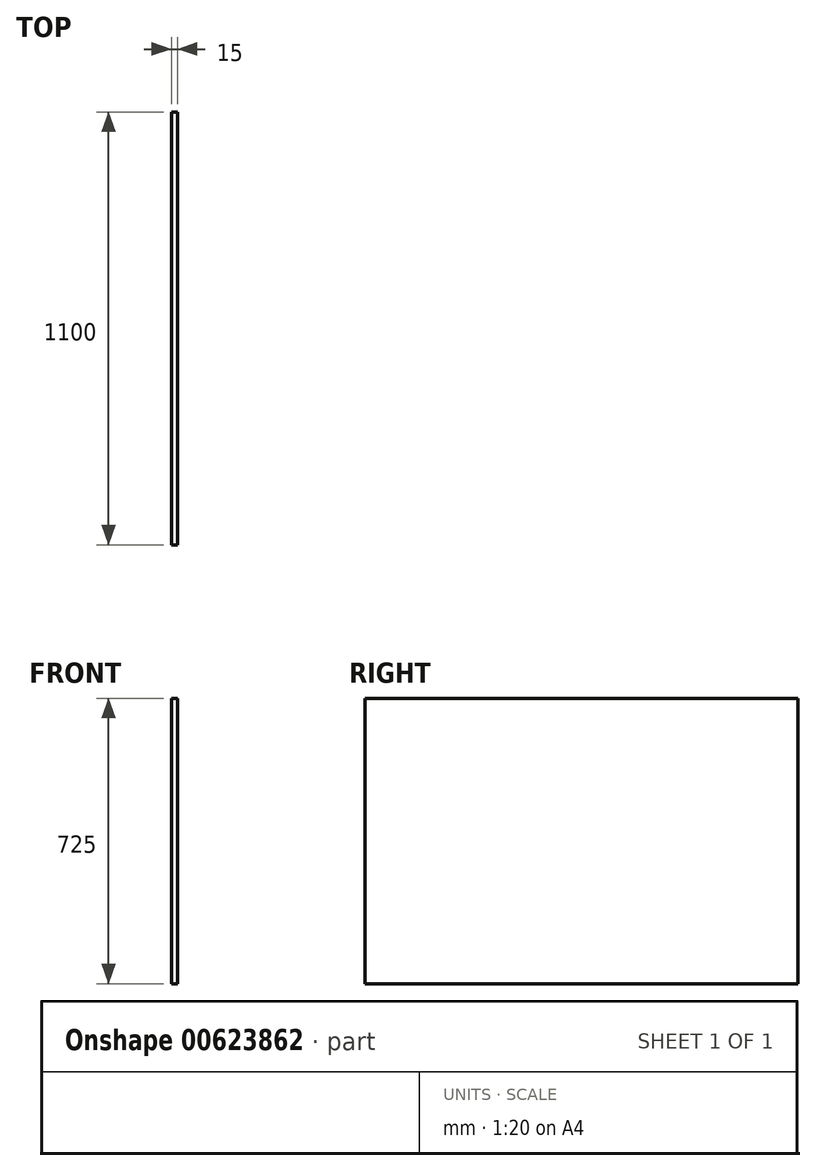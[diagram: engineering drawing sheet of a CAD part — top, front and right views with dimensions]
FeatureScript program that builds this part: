
annotation { "Feature Type Name" : "Feature", "Feature Type Description" : "" }
export const myFeature = defineFeature(function(context is Context, id is Id, definition is map)
    precondition{}
    {
        {
            var Q0;
            Q0=qCreatedBy(makeId("Top.planeOp"),FACE);
            var sketch = newSketch(context, id + "F0", { "sketchPlane" : qUnion([Q0])});
            skLineSegment(sketch, "E0.bottom", {"start": v(0, 1100) * mm, "end": v(15, 1100) * mm});
            skLineSegment(sketch, "E0.top", {"start": v(0, 0) * mm, "end": v(15, 0) * mm});
            skLineSegment(sketch, "E0.left", {"start": v(0, 1100) * mm, "end": v(0, 0) * mm});
            skLineSegment(sketch, "E0.right", {"start": v(15, 1100) * mm, "end": v(15, 0) * mm});
            skSolve(sketch);
        }
        {
            var Q0;
            Q0=qSketchRegion(id+"F0",true);
            extrude(context, id + "F1", {"entities" : qUnion([Q0]), "depth" : 725 * mm, "offsetDistance" : 25 * mm});
        }
    });
